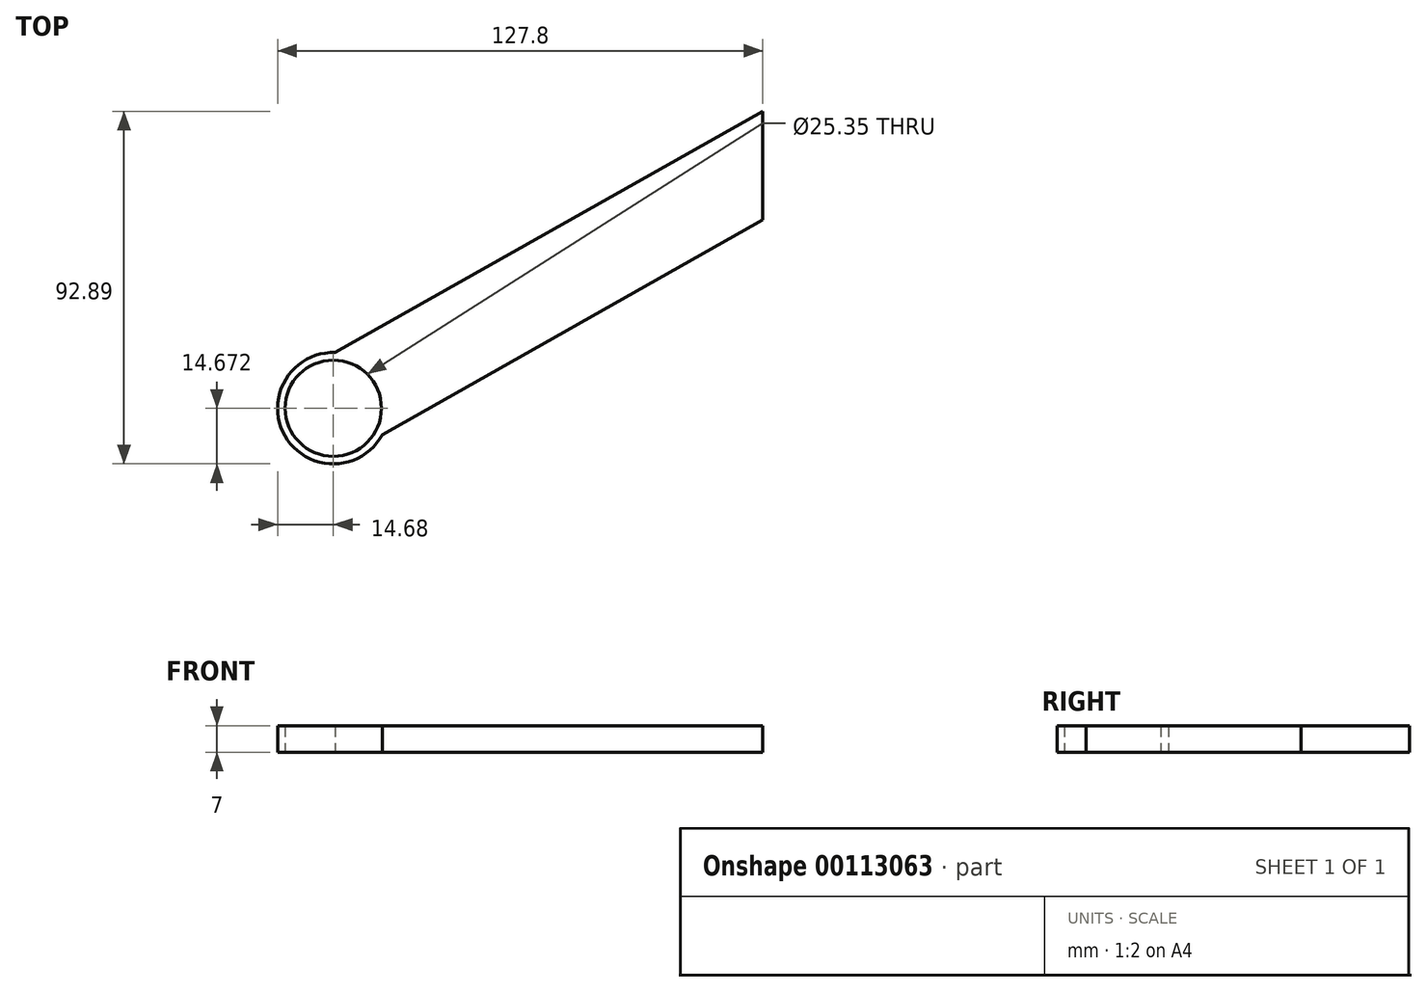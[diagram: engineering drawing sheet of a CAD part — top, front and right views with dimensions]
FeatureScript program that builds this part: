
annotation { "Feature Type Name" : "Feature", "Feature Type Description" : "" }
export const myFeature = defineFeature(function(context is Context, id is Id, definition is map)
    precondition{}
    {
        {
            var Q0;
            Q0=qCreatedBy(makeId("Top.planeOp"),FACE);
            var sketch = newSketch(context, id + "F0", { "sketchPlane" : qUnion([Q0])});
            skCircle(sketch, "E0", {"center": v(0, -49.6) * mm, "radius": 12.68 * mm});
            skLineSegment(sketch, "E1", {"start": v(-7.92, -39.7) * mm, "end": v(113.12, 28.62) * mm});
            skLineSegment(sketch, "E2", {"start": v(8.35, -59.14) * mm, "end": v(113.12, 0) * mm});
            skLineSegment(sketch, "E3", {"start": v(113.12, 0) * mm, "end": v(113.12, 28.62) * mm});
            skLineSegment(sketch, "E4", {"start": v(11.01, -43.32) * mm, "end": v(113.12, 14.3) * mm});
            skCircle(sketch, "E5.0", {"center": v(0, -49.6) * mm, "radius": 14.68 * mm});
            skSolve(sketch);
        }
        {
            var Q0;
            Q0 = qSketchRegion(id + "F0", true);
            extrude(context, id + "F1", {"entities" : qUnion([Q0]), "depth" : 7 * mm});
        }
    });
